# Revit family: SP4182W_EUR_Revit
name_source: partatom
category: Mechanical Equipment
revit_build: Autodesk Revit 2014 (Build: 20130215_1615(x64)
units: mm (PartAtom-declared; Revit-internal decimal feet)

## types (1)
- Standard
    Connector_22_Diameter = 0' - 0"
    Connector_23_Diameter = 0' - 0"
    Connector_24_Diameter = 0' - 0"
    Connector_29_Diameter = 0' - 0"
    Connector_30_Diameter = 0' - 0"
    Connector_31_Diameter = 0' - 0"
    Connector_32_Diameter = 0' - 0"
    Connector_33_Diameter = 0' - 0"
    Connector_34_Diameter = 0' - 0"
    Description = Electric Resistive Humidifier Weather proof
    Manufacturer = Neptronic
    Model = SKE10-W, SKE20-W, SKE30-W, SKE40-W
    Part Number = SP4182W
    URL = www.neptronic.com
    d170 = 0' - 0 1/4"
    d172 = 0' - 0 1/4"
    d174 = 0' - 0 1/4"
    d176 = 0' - 0 1/4"
    d178 = 0' - 0 1/4"
    d180 = 0' - 0 1/4"
    d182 = 0' - 1 7/16"
    d184 = 0' - 1 7/16"
    d186 = 0' - 0 1/4"
    d188 = 0' - 0 1/8"
    d190 = 0' - 0 3/32"
    d192 = 0' - 0 3/32"
    d194 = 0' - 0 1/8"
    d196 = 0' - 0 1/4"
    d198 = 0' - 0 1/4"
    d200 = 2' - 1 7/8"
    d202 = 2' - 3 7/8"
    d204 = 2' - 10 15/32"
    d206 = 0' - 0 3/16"
    d208 = 0' - 0 1/16"

## geometry (parser evidence)
native form markers: Sweep x1
no freeform markers — native parametric forms only
